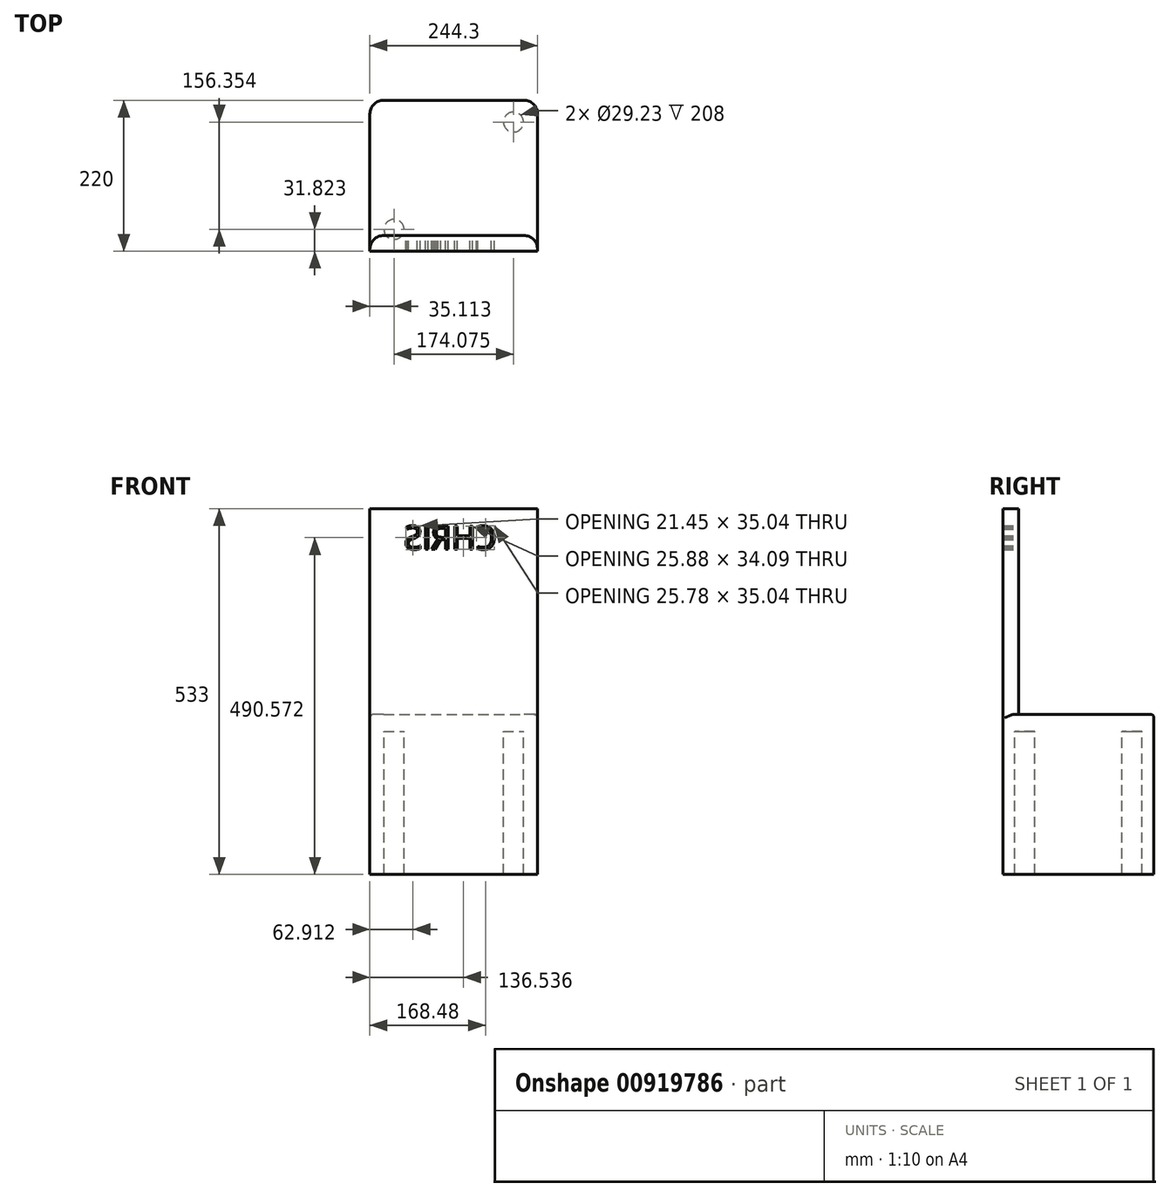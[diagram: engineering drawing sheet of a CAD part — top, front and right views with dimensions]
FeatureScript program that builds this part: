
annotation { "Feature Type Name" : "Feature", "Feature Type Description" : "" }
export const myFeature = defineFeature(function(context is Context, id is Id, definition is map)
    precondition{}
    {
        {
            var Q0;
            Q0=qCreatedBy(makeId("Top.planeOp"),FACE);
            var sketch = newSketch(context, id + "F0", { "sketchPlane" : qUnion([Q0])});
            skLineSegment(sketch, "E0.bottom", {"start": v(122.15, -110) * mm, "end": v(-122.15, -110) * mm});
            skLineSegment(sketch, "E0.top", {"start": v(102.15, 110) * mm, "end": v(-102.15, 110) * mm});
            skLineSegment(sketch, "E0.left", {"start": v(122.15, -110) * mm, "end": v(122.15, 90) * mm});
            skLineSegment(sketch, "E0.right", {"start": v(-122.15, -110) * mm, "end": v(-122.15, 90) * mm});
            skPoint(sketch, "E0.middle", {"position": v(0, 0) * mm});
            skPoint(sketch, "E1.visualSharp", {"position": v(-122.15, 110) * mm});
            skArc(sketch, "E1.filletArc", {"start": v(-102.15, 110) * mm, "mid": v(-116.3, 104.14) * mm, "end": v(-122.15, 90) * mm});
            skPoint(sketch, "E2.visualSharp", {"position": v(122.15, 110) * mm});
            skArc(sketch, "E2.filletArc", {"start": v(122.15, 90) * mm, "mid": v(116.3, 104.14) * mm, "end": v(102.15, 110) * mm});
            skSolve(sketch);
        }
        {
            var Q0;
            Q0 = qSketchRegion(id + "F0", true);
            extrude(context, id + "F1", {"entities" : qUnion([Q0]), "depth" : 25 * mm, "offsetDistance" : 25 * mm});
        }
        {
            var Q0;
            Q0=makeQuery(id+"F1.opExtrude","CAP_FACE",FACE,{"disambiguationData":[OSD([sQuery(id+"F0.wireOp",EDGE,"E0.bottom"),sQuery(id+"F0.wireOp",EDGE,"E0.top"),sQuery(id+"F0.wireOp",EDGE,"E0.left"),sQuery(id+"F0.wireOp",EDGE,"E0.right"),sQuery(id+"F0.wireOp",EDGE,"E1.filletArc"),sQuery(id+"F0.wireOp",EDGE,"E2.filletArc")])],"isStart":false});
            var sketch = newSketch(context, id + "F2", { "sketchPlane" : qUnion([Q0])});
            skLineSegment(sketch, "E3.bottom", {"start": v(-122.15, -110) * mm, "end": v(122.15, -110) * mm});
            skLineSegment(sketch, "E3.top", {"start": v(-102.15, -87.1) * mm, "end": v(102.15, -87.1) * mm});
            skLineSegment(sketch, "E3.left", {"start": v(-122.15, -110) * mm, "end": v(-122.15, -107.1) * mm});
            skLineSegment(sketch, "E3.right", {"start": v(122.15, -110) * mm, "end": v(122.15, -107.1) * mm});
            skPoint(sketch, "E4.visualSharp", {"position": v(122.15, -87.1) * mm});
            skArc(sketch, "E4.filletArc", {"start": v(122.15, -107.1) * mm, "mid": v(116.3, -92.97) * mm, "end": v(102.15, -87.1) * mm});
            skPoint(sketch, "E5.visualSharp", {"position": v(-122.15, -87.1) * mm});
            skArc(sketch, "E5.filletArc", {"start": v(-102.15, -87.1) * mm, "mid": v(-116.3, -92.97) * mm, "end": v(-122.15, -107.1) * mm});
            skSolve(sketch);
        }
        {
            var Q0;
            Q0 = qSketchRegion(id + "F2", true);
            extrude(context, id + "F3", {"entities" : qUnion([Q0]), "operationType" : NewBodyOperationType.ADD, "depth" : 300 * mm, "offsetDistance" : 25 * mm});
        }
        {
            var Q0;
            Q0=makeQuery(id+"F1.opExtrude","CAP_FACE",FACE,{"disambiguationData":[OSD([sQuery(id+"F0.wireOp",EDGE,"E0.bottom"),sQuery(id+"F0.wireOp",EDGE,"E0.top"),sQuery(id+"F0.wireOp",EDGE,"E0.left"),sQuery(id+"F0.wireOp",EDGE,"E0.right"),sQuery(id+"F0.wireOp",EDGE,"E1.filletArc"),sQuery(id+"F0.wireOp",EDGE,"E2.filletArc")])],"isStart":true});
            var sketch = newSketch(context, id + "F4", { "sketchPlane" : qUnion([Q0])});
            skCircle(sketch, "E6", {"center": v(-87.04, -78.18) * mm, "radius": 14.61 * mm});
            skCircle(sketch, "E7.MirrorC", {"center": v(87.04, -78.18) * mm, "radius": 14.61 * mm});
            skCircle(sketch, "E8.MirrorC", {"center": v(87.04, 78.18) * mm, "radius": 14.61 * mm});
            skCircle(sketch, "E9.MirrorC", {"center": v(-87.04, 78.18) * mm, "radius": 14.61 * mm});
            skSolve(sketch);
        }
        {
            var Q0;
            Q0=makeQuery(id+"F4.imprint","IMPRINT",FACE,{"disambiguationData":[TD([[makeQuery(id+"F4.imprint","IMPRINT",EDGE,{"derivedFrom":sQuery(id+"F4.wireOp",EDGE,"E6")}),1.0]])]});
            var Q1;
            Q1=makeQuery(id+"F4.imprint","IMPRINT",FACE,{"disambiguationData":[TD([[makeQuery(id+"F4.imprint","IMPRINT",EDGE,{"derivedFrom":sQuery(id+"F4.wireOp",EDGE,"E7.MirrorC")}),-1.0]])]});
            var Q2;
            Q2=makeQuery(id+"F4.imprint","IMPRINT",FACE,{"disambiguationData":[TD([[makeQuery(id+"F4.imprint","IMPRINT",EDGE,{"derivedFrom":sQuery(id+"F4.wireOp",EDGE,"E8.MirrorC")}),1.0]])]});
            var Q3;
            Q3=makeQuery(id+"F4.imprint","IMPRINT",FACE,{"disambiguationData":[TD([[makeQuery(id+"F4.imprint","IMPRINT",EDGE,{"derivedFrom":sQuery(id+"F4.wireOp",EDGE,"E9.MirrorC")}),-1.0]])]});
            extrude(context, id + "F5", {"entities" : qUnion([Q0, Q1, Q2, Q3]), "operationType" : NewBodyOperationType.ADD, "depth" : 208 * mm, "offsetDistance" : 25 * mm});
        }
        {
            var Q0;
            Q0=makeQuery(id+"F1.opExtrude","CAP_EDGE",EDGE,{"disambiguationData":[OSD([sQuery(id+"F0.wireOp",EDGE,"E0.top")])],"isStart":false});
            var Q1;
            Q1=makeQuery(id+"F1.opExtrude","CAP_EDGE",EDGE,{"disambiguationData":[OSD([sQuery(id+"F0.wireOp",EDGE,"E0.top")])],"isStart":true});
            fillet(context, id + "F6", {"entities" : qUnion([Q0, Q1]), "radius" : 5 * mm, "tangentPropagation" : true, "allowEdgeOverflow" : false});
        }
        {
            var Q0;
            Q0=makeQuery(id+"F3.opExtrude","SWEPT_FACE",FACE,{"disambiguationData":[OSD([sQuery(id+"F2.wireOp",EDGE,"E3.top")])]});
            var sketch = newSketch(context, id + "F7", { "sketchPlane" : qUnion([Q0])});
            skText(sketch, "E10", { "text": "CHRIS", "fontName": "OpenSans-Regular.ttf"});
            const initialGuessF7  = {"E10": [-0.06214, 0.26552, 1, 0, 0.03438]};
            skSetInitialGuess(sketch, initialGuessF7);
            skSolve(sketch);
        }
        {
            var Q0;
            Q0=makeQuery(id+"F7.imprint","IMPRINT",FACE,{"disambiguationData":[TD([[makeQuery(id+"F7.imprint","IMPRINT",EDGE,{"derivedFrom":sQuery(id+"F7.wireOp",EDGE,"E10.sketch_text.stroke-45")}),-1.0]])]});
            var Q1;
            Q1=makeQuery(id+"F7.imprint","IMPRINT",FACE,{"disambiguationData":[TD([[makeQuery(id+"F7.imprint","IMPRINT",EDGE,{"derivedFrom":sQuery(id+"F7.wireOp",EDGE,"E10.sketch_text.stroke-49")}),-1.0]])]});
            var Q2;
            Q2=makeQuery(id+"F7.imprint","IMPRINT",FACE,{"disambiguationData":[TD([[makeQuery(id+"F7.imprint","IMPRINT",EDGE,{"derivedFrom":sQuery(id+"F7.wireOp",EDGE,"E10.sketch_text.stroke-27")}),-1.0]])]});
            var Q3;
            Q3=makeQuery(id+"F7.imprint","IMPRINT",FACE,{"disambiguationData":[TD([[makeQuery(id+"F7.imprint","IMPRINT",EDGE,{"derivedFrom":sQuery(id+"F7.wireOp",EDGE,"E10.sketch_text.stroke-15")}),-1.0]])]});
            var Q4;
            Q4=makeQuery(id+"F7.imprint","IMPRINT",FACE,{"disambiguationData":[TD([[makeQuery(id+"F7.imprint","IMPRINT",EDGE,{"derivedFrom":sQuery(id+"F7.wireOp",EDGE,"E10.sketch_text.stroke-0")}),-1.0]])]});
            extrude(context, id + "F8", {"entities" : qUnion([Q0, Q1, Q2, Q3, Q4]), "operationType" : NewBodyOperationType.REMOVE, "endBound" : BoundingType.THROUGH_ALL, "oppositeDirection" : true, "depth" : 25 * mm, "offsetDistance" : 25 * mm});
        }
    });
